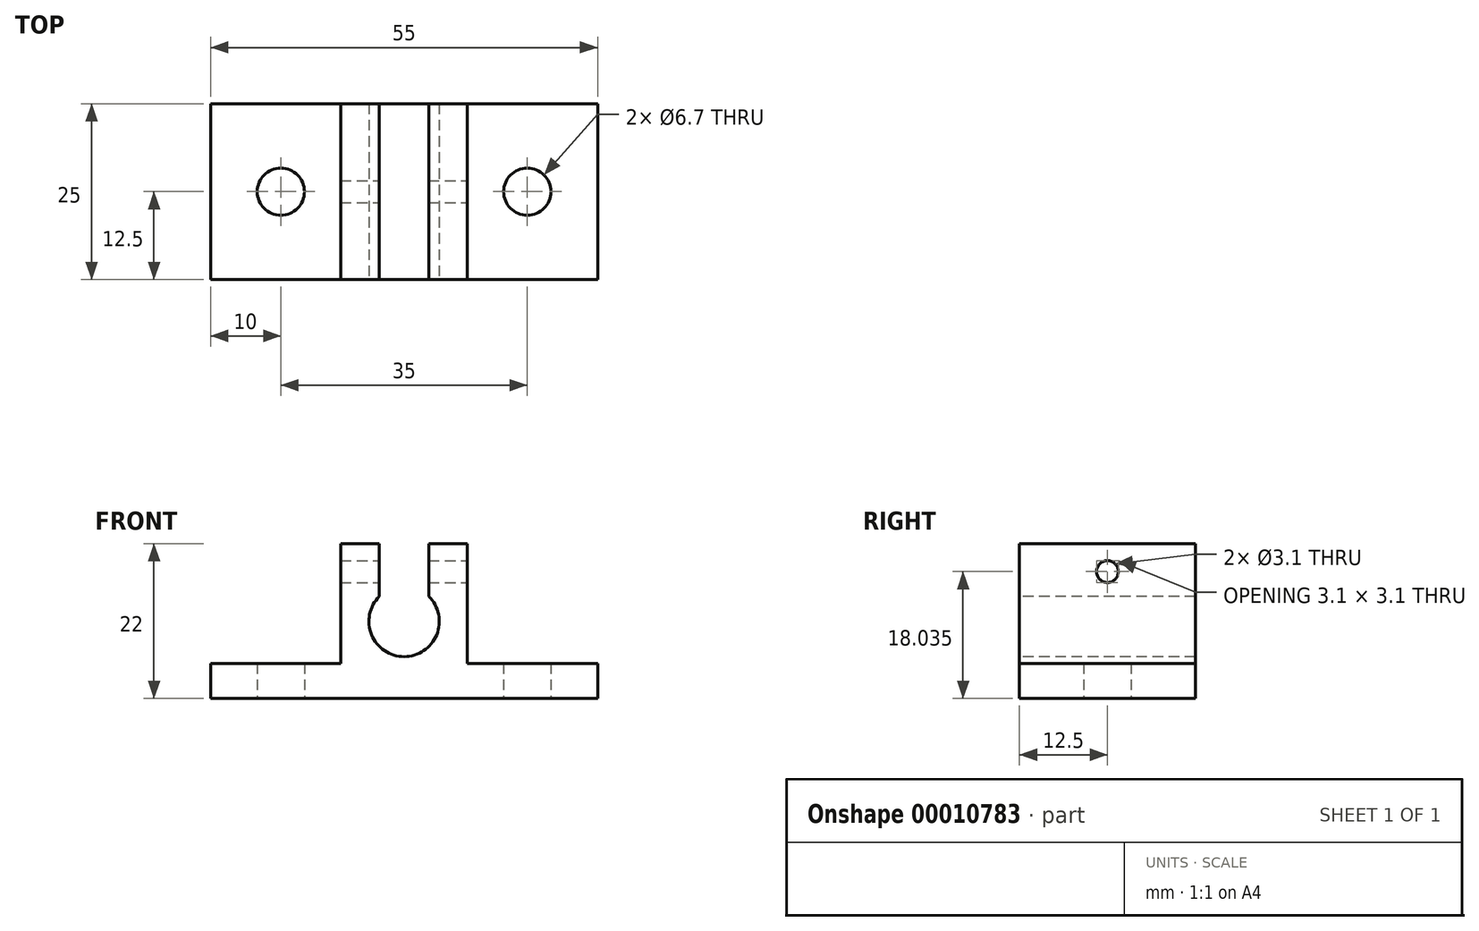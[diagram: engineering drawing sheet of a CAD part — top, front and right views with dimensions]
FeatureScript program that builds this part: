
annotation { "Feature Type Name" : "Feature", "Feature Type Description" : "" }
export const myFeature = defineFeature(function(context is Context, id is Id, definition is map)
    precondition{}
    {
        {
            var Q0;
            Q0=qCreatedBy(makeId("Top.planeOp"),FACE);
            var sketch = newSketch(context, id + "F0", { "sketchPlane" : qUnion([Q0])});
            skLineSegment(sketch, "E0.bottom", {"start": v(-27.5, 12.5) * mm, "end": v(27.5, 12.5) * mm});
            skLineSegment(sketch, "E0.top", {"start": v(-27.5, -12.5) * mm, "end": v(27.5, -12.5) * mm});
            skLineSegment(sketch, "E0.left", {"start": v(-27.5, 12.5) * mm, "end": v(-27.5, -12.5) * mm});
            skLineSegment(sketch, "E0.right", {"start": v(27.5, 12.5) * mm, "end": v(27.5, -12.5) * mm});
            skCircle(sketch, "E1", {"center": v(-17.5, 0) * mm, "radius": 3.35 * mm});
            skCircle(sketch, "E2", {"center": v(17.5, 0) * mm, "radius": 3.35 * mm});
            skSolve(sketch);
        }
        {
            var Q0;
            Q0 = qSketchRegion(id + "F0", true);
            extrude(context, id + "F1", {"entities" : qUnion([Q0]), "depth" : 5 * mm});
        }
        {
            var Q0;
            Q0=makeQuery(id+"F1.opExtrude","CAP_FACE",FACE,{"disambiguationData":[OSD([sQuery(id+"F0.wireOp",EDGE,"E0.bottom"),sQuery(id+"F0.wireOp",EDGE,"E0.top"),sQuery(id+"F0.wireOp",EDGE,"E0.left"),sQuery(id+"F0.wireOp",EDGE,"E0.right"),sQuery(id+"F0.wireOp",EDGE,"E1"),sQuery(id+"F0.wireOp",EDGE,"E2")])],"isStart":false});
            var sketch = newSketch(context, id + "F2", { "sketchPlane" : qUnion([Q0])});
            skLineSegment(sketch, "E3.bottom", {"start": v(-9, 12.5) * mm, "end": v(9, 12.5) * mm});
            skLineSegment(sketch, "E3.top", {"start": v(-9, -12.5) * mm, "end": v(9, -12.5) * mm});
            skLineSegment(sketch, "E3.left", {"start": v(-9, 12.5) * mm, "end": v(-9, -12.5) * mm});
            skLineSegment(sketch, "E3.right", {"start": v(9, 12.5) * mm, "end": v(9, -12.5) * mm});
            skSolve(sketch);
        }
        {
            var Q0;
            Q0 = qSketchRegion(id + "F2", true);
            extrude(context, id + "F3", {"entities" : qUnion([Q0]), "operationType" : NewBodyOperationType.ADD, "depth" : 17 * mm});
        }
        {
            var Q0;
            Q0=makeQuery(id+"F3.boolean.opBoolean","MERGE",FACE,{"derivedFrom":[makeQuery(id+"F1.opExtrude","SWEPT_FACE",FACE,{"disambiguationData":[OSD([sQuery(id+"F0.wireOp",EDGE,"E0.top")])]}),makeQuery(id+"F3.opExtrude","SWEPT_FACE",FACE,{"disambiguationData":[OSD([sQuery(id+"F2.wireOp",EDGE,"E3.top")])]})]});
            var sketch = newSketch(context, id + "F4", { "sketchPlane" : qUnion([Q0])});
            skCircle(sketch, "E4", {"center": v(0, 10.94) * mm, "radius": 5 * mm});
            skPoint(sketch, "E4.centerSnap0", {"position": v(9, 13.5) * mm});
            skSolve(sketch);
        }
        {
            var Q0;
            Q0 = qSketchRegion(id + "F4", true);
            extrude(context, id + "F5", {"entities" : qUnion([Q0]), "operationType" : NewBodyOperationType.REMOVE, "oppositeDirection" : true, "depth" : 25 * mm});
        }
        {
            var Q0;
            Q0=makeQuery(id+"F3.opExtrude","CAP_FACE",FACE,{"disambiguationData":[OSD([sQuery(id+"F2.wireOp",EDGE,"E3.bottom"),sQuery(id+"F2.wireOp",EDGE,"E3.top"),sQuery(id+"F2.wireOp",EDGE,"E3.left"),sQuery(id+"F2.wireOp",EDGE,"E3.right")])],"isStart":false});
            var sketch = newSketch(context, id + "F6", { "sketchPlane" : qUnion([Q0])});
            skLineSegment(sketch, "E5.bottom", {"start": v(-3.5, 12.5) * mm, "end": v(3.5, 12.5) * mm});
            skLineSegment(sketch, "E5.top", {"start": v(-3.5, -12.5) * mm, "end": v(3.5, -12.5) * mm});
            skLineSegment(sketch, "E5.left", {"start": v(-3.5, 12.5) * mm, "end": v(-3.5, -12.5) * mm});
            skLineSegment(sketch, "E5.right", {"start": v(3.5, 12.5) * mm, "end": v(3.5, -12.5) * mm});
            skLineSegment(sketch, "E6.bottom", {"start": v(111.69, -55.78) * mm, "end": v(114, -55.78) * mm});
            skLineSegment(sketch, "E6.top", {"start": v(111.69, -53.62) * mm, "end": v(114, -53.62) * mm});
            skLineSegment(sketch, "E6.left", {"start": v(111.69, -55.78) * mm, "end": v(111.69, -53.62) * mm});
            skLineSegment(sketch, "E6.right", {"start": v(114, -55.78) * mm, "end": v(114, -53.62) * mm});
            skSolve(sketch);
        }
        {
            var Q0;
            Q0 = qSketchRegion(id + "F6", true);
            extrude(context, id + "F7", {"entities" : qUnion([Q0]), "operationType" : NewBodyOperationType.REMOVE, "oppositeDirection" : true, "depth" : 8 * mm});
        }
        {
            var Q0;
            Q0=makeQuery(id+"F3.opExtrude","SWEPT_FACE",FACE,{"disambiguationData":[OSD([sQuery(id+"F2.wireOp",EDGE,"E3.right")])]});
            var sketch = newSketch(context, id + "F8", { "sketchPlane" : qUnion([Q0])});
            skCircle(sketch, "E7", {"center": v(0, 18.04) * mm, "radius": 1.55 * mm});
            skSolve(sketch);
        }
        {
            var Q0;
            Q0 = qSketchRegion(id + "F8", true);
            extrude(context, id + "F9", {"entities" : qUnion([Q0]), "operationType" : NewBodyOperationType.REMOVE, "oppositeDirection" : true, "depth" : 25 * mm});
        }
    });
